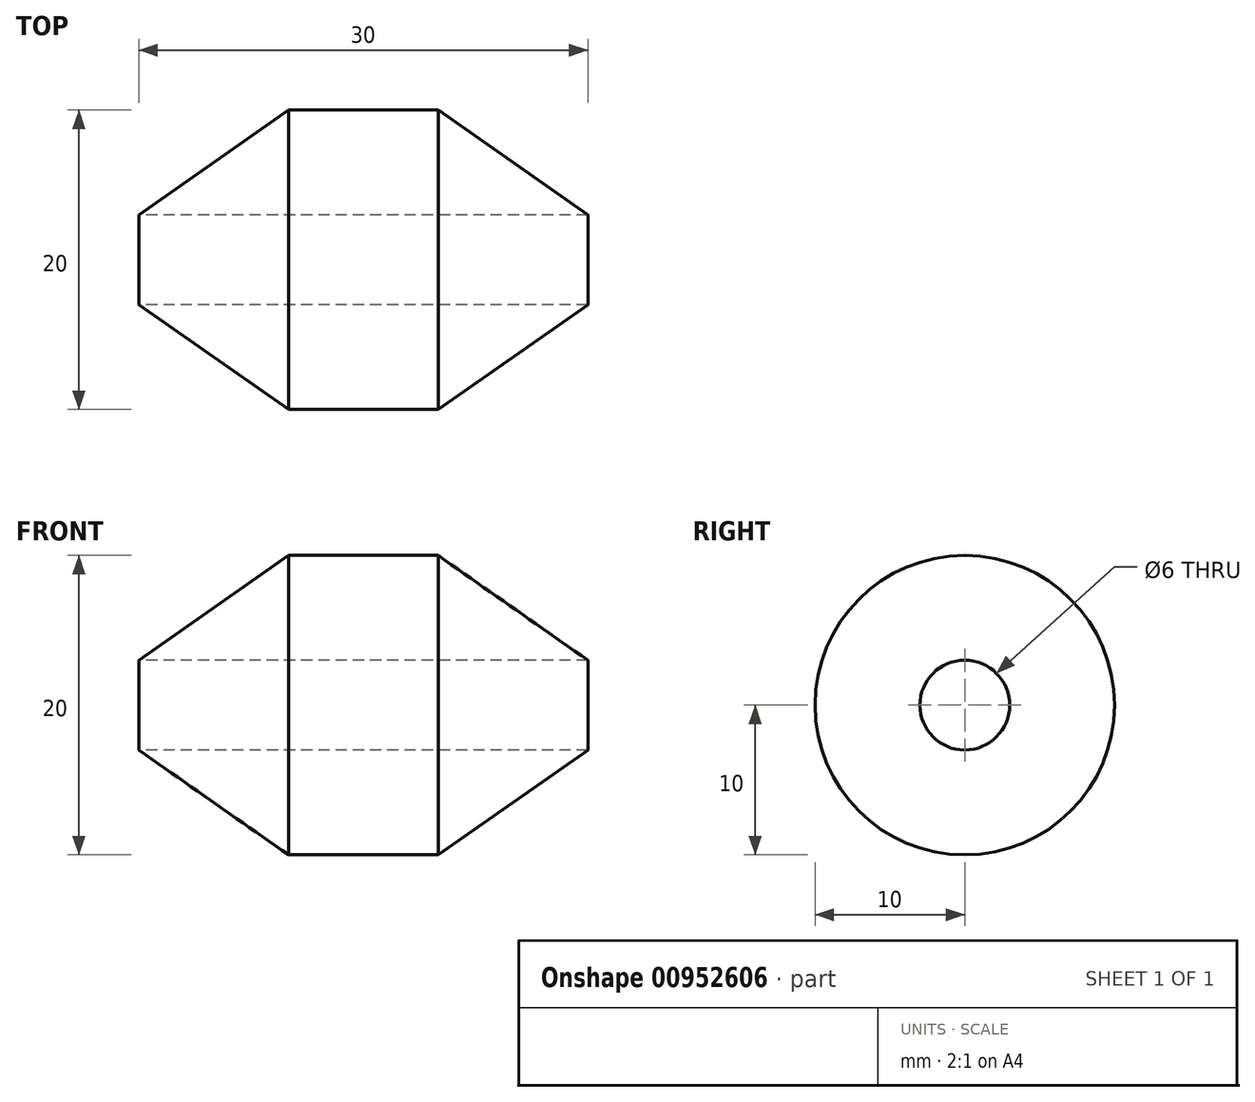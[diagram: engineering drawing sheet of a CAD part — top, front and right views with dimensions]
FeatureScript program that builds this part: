
annotation { "Feature Type Name" : "Feature", "Feature Type Description" : "" }
export const myFeature = defineFeature(function(context is Context, id is Id, definition is map)
    precondition{}
    {
        {
            var Q0;
            Q0=qCreatedBy(makeId("Front.planeOp"),FACE);
            var sketch = newSketch(context, id + "F0", { "sketchPlane" : qUnion([Q0])});
            skLineSegment(sketch, "E0", {"start": v(0, 0) * mm, "end": v(0, 10) * mm});
            skLineSegment(sketch, "E1", {"start": v(0, 10) * mm, "end": v(5, 10) * mm});
            skLineSegment(sketch, "E2", {"start": v(5, 10) * mm, "end": v(15, 3) * mm});
            skLineSegment(sketch, "E3", {"start": v(15, 3) * mm, "end": v(15, 0) * mm});
            skLineSegment(sketch, "E4", {"start": v(15, 0) * mm, "end": v(0, 0) * mm});
            skSolve(sketch);
        }
        {
            var Q0;
            Q0=makeQuery(id+"F0.imprint","IMPRINT",FACE,{"disambiguationData":[TD([[makeQuery(id+"F0.imprint","IMPRINT",EDGE,{"derivedFrom":sQuery(id+"F0.wireOp",EDGE,"E0")}),-1.0]])]});
            var Q1;
            Q1=sQuery(id+"F0.wireOp",EDGE,"E4");
            revolve(context, id + "F1", {"surfaceOperationType" : NewSurfaceOperationType.NEW, "entities" : qUnion([Q0]), "axis" : qUnion([Q1]), "revolveType" : RevolveType.FULL});
        }
        {
            var Q0;
            Q0=makeQuery(id+"F1.opRevolve","SWEPT_BODY",BODY,{"disambiguationData":[OSD([sQuery(id+"F0.wireOp",EDGE,"E0"),sQuery(id+"F0.wireOp",EDGE,"E1"),sQuery(id+"F0.wireOp",EDGE,"E2"),sQuery(id+"F0.wireOp",EDGE,"E3"),sQuery(id+"F0.wireOp",EDGE,"E4")])]});
            var Q1;
            Q1=qCreatedBy(makeId("Right.planeOp"),FACE);
            mirror(context, id + "F2", {"operationType" : NewBodyOperationType.ADD, "entities" : qUnion([Q0]), "mirrorPlane" : qUnion([Q1])});
        }
        {
            var Q0;
            Q0=makeQuery(id+"F2.opPattern","COPY",FACE,{"derivedFrom":makeQuery(id+"F1.opRevolve","SWEPT_FACE",FACE,{"disambiguationData":[OSD([sQuery(id+"F0.wireOp",EDGE,"E3")])]}),"instanceName":"1"});
            var sketch = newSketch(context, id + "F3", { "sketchPlane" : qUnion([Q0])});
            skCircle(sketch, "E5", {"center": v(0, 0) * mm, "radius": 3 * mm});
            skSolve(sketch);
        }
        {
            var Q0;
            Q0 = qSketchRegion(id + "F3", true);
            extrude(context, id + "F4", {"entities" : qUnion([Q0]), "operationType" : NewBodyOperationType.REMOVE, "endBound" : BoundingType.THROUGH_ALL, "oppositeDirection" : true, "depth" : 25 * mm, "offsetDistance" : 25 * mm});
        }
    });
